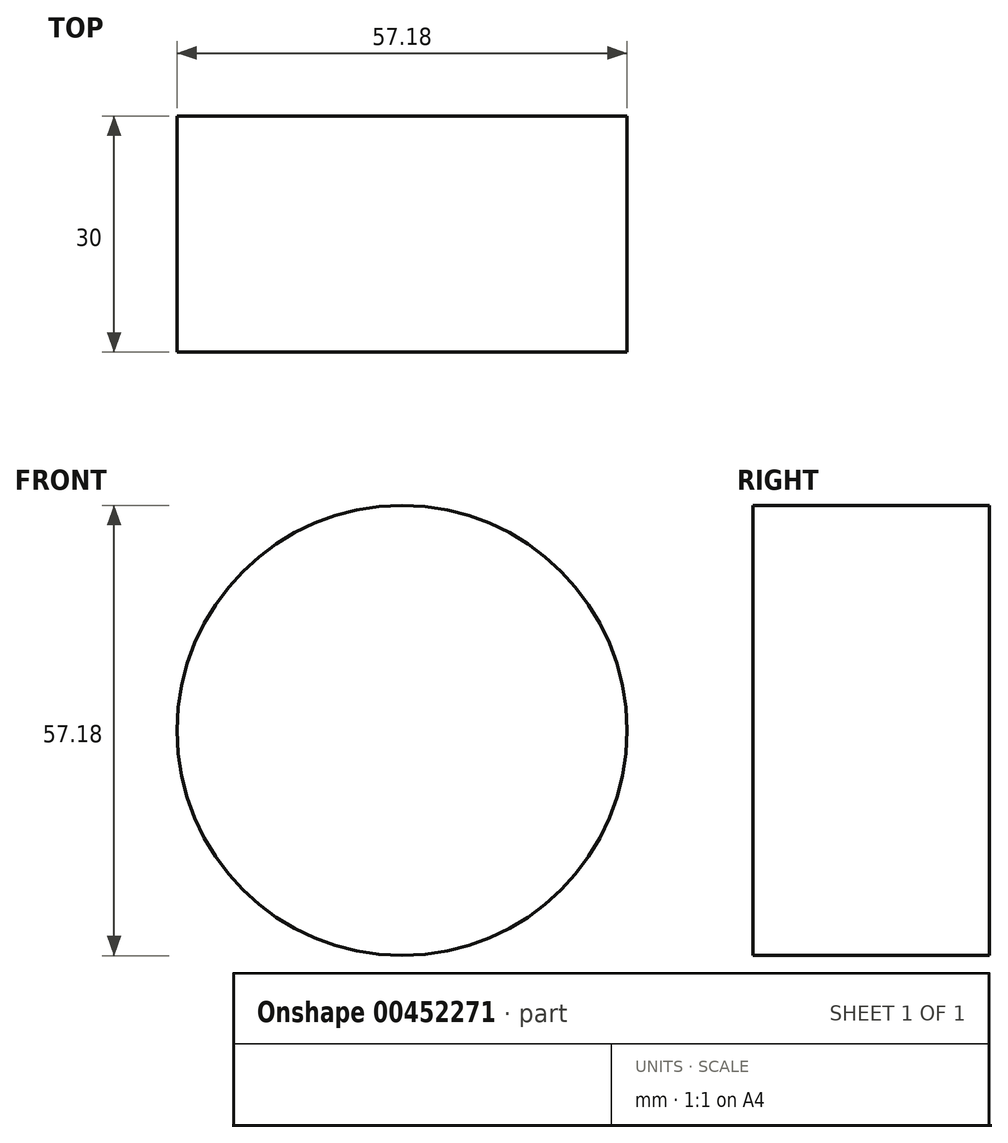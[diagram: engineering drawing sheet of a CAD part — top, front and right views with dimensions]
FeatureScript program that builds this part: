
annotation { "Feature Type Name" : "Feature", "Feature Type Description" : "" }
export const myFeature = defineFeature(function(context is Context, id is Id, definition is map)
    precondition{}
    {
        {
            var Q0;
            Q0=qCreatedBy(makeId("Front.planeOp"),FACE);
            var sketch = newSketch(context, id + "F0", { "sketchPlane" : qUnion([Q0])});
            skCircle(sketch, "E0", {"center": v(0, 0) * mm, "radius": 28.59 * mm});
            skSolve(sketch);
        }
        {
            var Q0;
            Q0=qSketchRegion(id+"F0",true);
            extrude(context, id + "F1", {"entities" : qUnion([Q0]), "depth" : 30 * mm});
        }
    });
